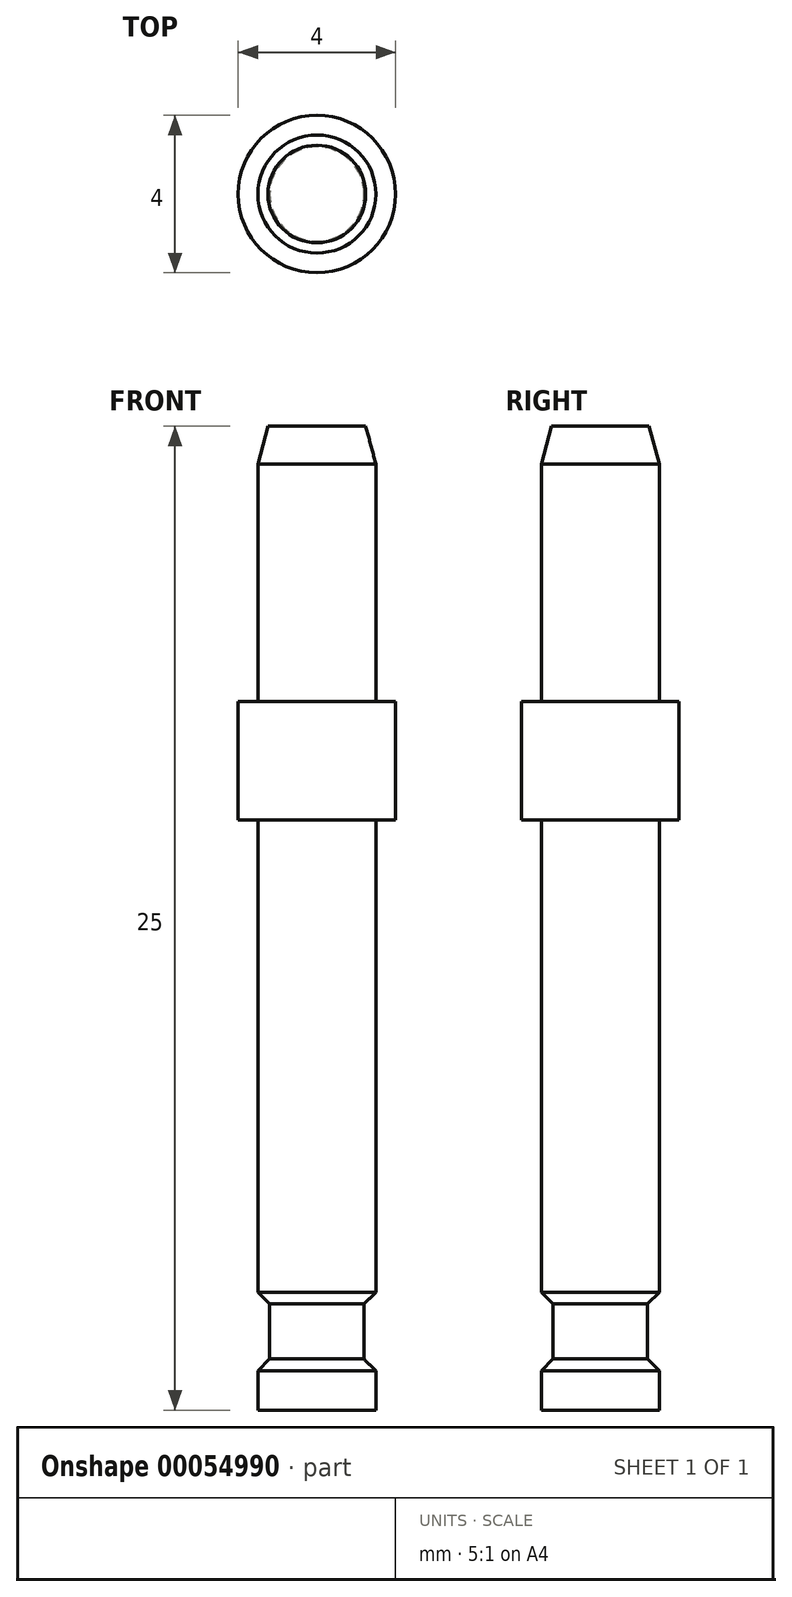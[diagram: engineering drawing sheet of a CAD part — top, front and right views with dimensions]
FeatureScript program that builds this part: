
annotation { "Feature Type Name" : "Feature", "Feature Type Description" : "" }
export const myFeature = defineFeature(function(context is Context, id is Id, definition is map)
    precondition{}
    {
        {
            var Q0;
            Q0=qCreatedBy(makeId("Front.planeOp"),FACE);
            var sketch = newSketch(context, id + "F0", { "sketchPlane" : qUnion([Q0])});
            skLineSegment(sketch, "E0", {"start": v(0, 0) * mm, "end": v(1.5, 0) * mm});
            skLineSegment(sketch, "E1", {"start": v(1.5, 0) * mm, "end": v(1.5, 1) * mm});
            skLineSegment(sketch, "E2", {"start": v(1.5, 1) * mm, "end": v(1.2, 1.3) * mm});
            skLineSegment(sketch, "E3", {"start": v(1.2, 1.3) * mm, "end": v(1.2, 2.7) * mm});
            skLineSegment(sketch, "E4", {"start": v(1.2, 2.7) * mm, "end": v(1.5, 3) * mm});
            skLineSegment(sketch, "E5", {"start": v(1.5, 3) * mm, "end": v(1.5, 15) * mm});
            skLineSegment(sketch, "E6", {"start": v(1.5, 15) * mm, "end": v(2, 15) * mm});
            skLineSegment(sketch, "E7", {"start": v(2, 15) * mm, "end": v(2, 18) * mm});
            skLineSegment(sketch, "E8", {"start": v(2, 18) * mm, "end": v(1.5, 18) * mm});
            skLineSegment(sketch, "E9", {"start": v(1.5, 18) * mm, "end": v(1.5, 24.03) * mm});
            skLineSegment(sketch, "E10", {"start": v(1.5, 24.03) * mm, "end": v(1.24, 25) * mm});
            skLineSegment(sketch, "E11", {"start": v(1.24, 25) * mm, "end": v(0, 25) * mm});
            skLineSegment(sketch, "E12", {"start": v(0, 25) * mm, "end": v(0, 0) * mm});
            skSolve(sketch);
        }
        {
            var Q0;
            Q0 = qSketchRegion(id + "F0", true);
            var Q1;
            Q1=sQuery(id+"F0.wireOp",EDGE,"E12");
            revolve(context, id + "F1", {"entities" : qUnion([Q0]), "axis" : qUnion([Q1]), "revolveType" : RevolveType.FULL});
        }
    });
